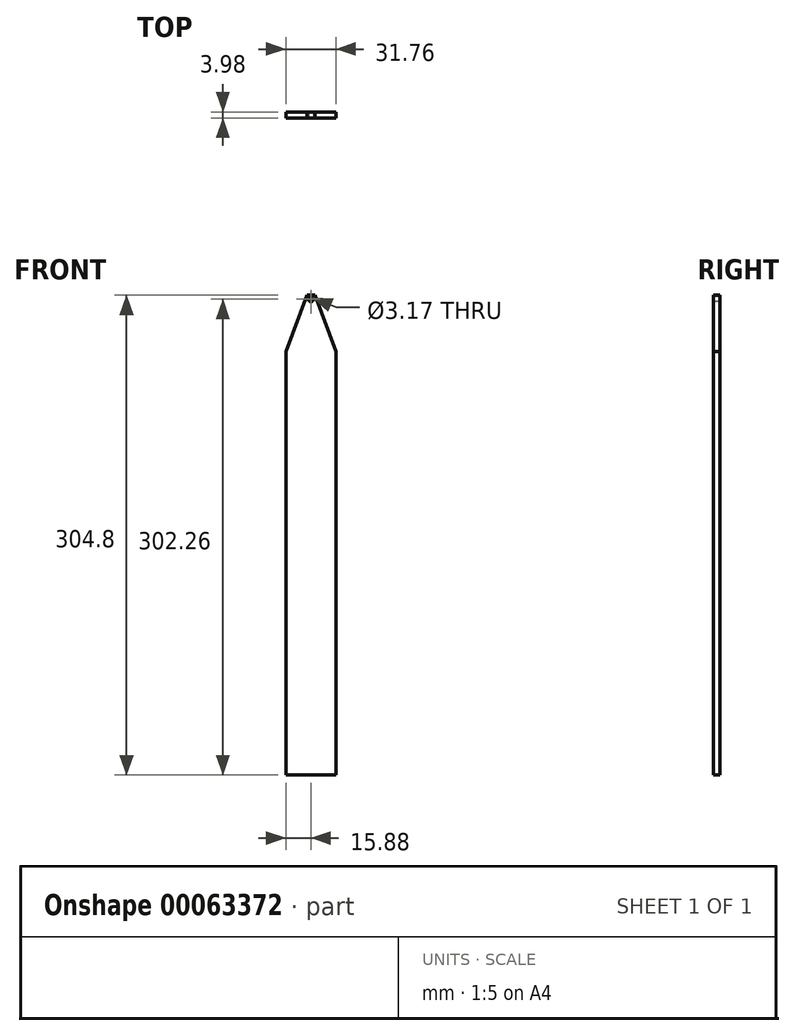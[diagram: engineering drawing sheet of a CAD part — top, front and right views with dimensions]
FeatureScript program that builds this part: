
annotation { "Feature Type Name" : "Feature", "Feature Type Description" : "" }
export const myFeature = defineFeature(function(context is Context, id is Id, definition is map)
    precondition{}
    {
        {
            var Q0;
            Q0=qCreatedBy(makeId("Top.planeOp"),FACE);
            var sketch = newSketch(context, id + "F0", { "sketchPlane" : qUnion([Q0])});
            skLineSegment(sketch, "E0.rect.bottom", {"start": v(15.87, 2) * mm, "end": v(-15.88, 2) * mm});
            skLineSegment(sketch, "E0.rect.top", {"start": v(15.87, -2) * mm, "end": v(-15.88, -2) * mm});
            skLineSegment(sketch, "E0.rect.left", {"start": v(15.87, 2) * mm, "end": v(15.87, -2) * mm});
            skLineSegment(sketch, "E0.rect.right", {"start": v(-15.88, 2) * mm, "end": v(-15.88, -2) * mm});
            skPoint(sketch, "E0.rect.middle", {"position": v(0, 0) * mm});
            skSolve(sketch);
        }
        {
            var Q0;
            Q0 = qSketchRegion(id + "F0", true);
            extrude(context, id + "F1", {"entities" : qUnion([Q0]), "endBound" : BoundingType.SYMMETRIC, "depth" : 304.8 * mm});
        }
        {
            var Q0;
            Q0=makeQuery(id+"F1.opExtrude","SWEPT_FACE",FACE,{"disambiguationData":[OSD([sQuery(id+"F0.wireOp",EDGE,"E0.rect.top")])]});
            var sketch = newSketch(context, id + "F2", { "sketchPlane" : qUnion([Q0])});
            skCircle(sketch, "E1", {"center": v(0, 149.86) * mm, "radius": 1.59 * mm});
            skLineSegment(sketch, "E2", {"start": v(-2.47, 152.4) * mm, "end": v(-15.88, 116.7) * mm});
            skLineSegment(sketch, "E3", {"start": v(-15.88, 116.7) * mm, "end": v(-15.88, 152.4) * mm});
            skLineSegment(sketch, "E4", {"start": v(-15.88, 152.4) * mm, "end": v(-2.47, 152.4) * mm});
            skLineSegment(sketch, "E5.MirrorCS", {"start": v(2.47, 152.4) * mm, "end": v(15.88, 116.7) * mm});
            skLineSegment(sketch, "E6.MirrorCS", {"start": v(15.88, 116.7) * mm, "end": v(15.88, 152.4) * mm});
            skLineSegment(sketch, "E7.MirrorCS", {"start": v(15.88, 152.4) * mm, "end": v(2.47, 152.4) * mm});
            skSolve(sketch);
        }
        {
            var Q0;
            Q0 = qSketchRegion(id + "F2", true);
            extrude(context, id + "F3", {"entities" : qUnion([Q0]), "operationType" : NewBodyOperationType.REMOVE, "endBound" : BoundingType.THROUGH_ALL, "oppositeDirection" : true, "depth" : 25.4 * mm});
        }
    });
